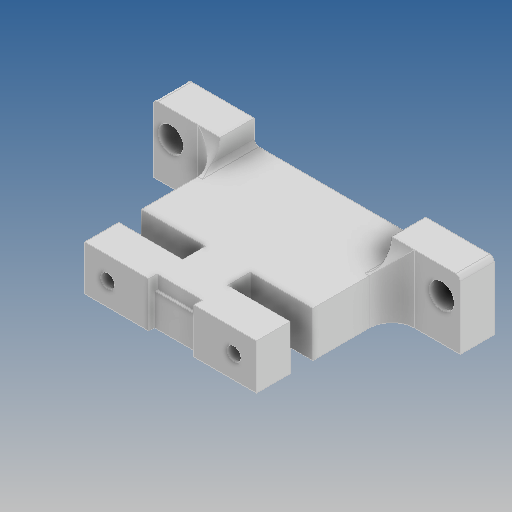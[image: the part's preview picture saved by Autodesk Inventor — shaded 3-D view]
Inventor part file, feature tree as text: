
AUTODESK INVENTOR PART (.ipt)
format: ipt  version: 2020 (Build 240168000, 168)  size: 226,304 bytes
history: native  units: mm
features: sketch x7, reference x7, extrude x5, fillet x4, other x3, hole x2
ambient origin geometry x8: Origin, YZ Plane, XZ Plane, XY Plane, X Axis, Y Axis, Z Axis, Center Point
bodies: Solid1 (feature_tree)
feature tree (28):
  extrude  "Extrusion1"  Depth=30.0mm
  extrude  "Extrusion2"  TaperAngle=0.0deg  [1 undecoded]
  fillet  "Fillet1"  Radius=2.0mm
  extrude  "Extrusion3"  Depth=10.0mm
  fillet  "Fillet2"  Radius=0.3mm
  extrude  "Extrusion4"  Depth=0.3mm
  hole  "Hole1"  [1 undecoded]
  extrude  "Extrusion5"  Depth=10.0mm
  fillet  "Fillet3"  Radius=15.0mm
  hole  "Hole2"  [1 undecoded]
  fillet  "Fillet4"  Radius=20.0mm
  sketch  "Sketch1"  dims[d0=136.0mm d1=30.0mm]
  sketch  "Sketch2"  dims[d2=15.0mm d3=0.0mm d4=0.0mm d5=0.0mm d6=2.0mm]
  reference  "Reference1"
  reference  "Reference3"
  reference  "Reference6"
  sketch  "Sketch3"  dims[d7=60.0mm d8=0.0mm d9=10.0mm d10=0.3mm]
  sketch  "Sketch5"  dims[d11=0.3mm d12=0.3mm]
  reference  "Reference8"
  reference  "Reference9"
  sketch  "Sketch6"  dims[d13=20.0mm d14=0.0mm d15=0.3mm]
  reference  "Reference10"
  reference  "Reference11"
  sketch  "Sketch7"  dims[d16=11.0mm d17=6.0mm d18=4.0mm d19=2.0mm d20=90.0deg d21=8.0mm d22=20.594885mm d23=10.0mm d24=15.0mm]
  sketch  "Sketch8"  dims[d25=27.698128mm d26=28.301872mm d27=20.0mm d28=0.0mm d29=2.0mm d30=10.0mm d31=10.0mm d32=6.0mm d33=6.0mm d34=4.0mm d35=2.0mm d36=90.0deg d37=8.0mm d38=20.594885mm d39=10.0mm]
  other  "30-00 Injectomat suplimentar.iam"
  other  "I.A.B 2.1 Aracet_Subansamble_Shrinkwrap_2:1"
  other  "0008-30-1009 Adaptor Ac:1"
note: 3 required parameter values undecoded (feature->parameter linkage not recoverable at this tier; creation-order binding heuristic only, values carry confidence <= 0.55)
